# Revit family: 511_AWN_DBS_nailfin
name_source: partatom
category: Windows
units: mm (PartAtom-declared; Revit-internal decimal feet)

## family parameters
Always vertical = Yes
Cut with Voids When Loaded = No
Host = Wall
OmniClass Number = 23.30.20.00
OmniClass Title = Windows
Room Calculation Point = No
Shared = No

## types (40) — shared parameters
Default Sill Height = 31 1/2"
Wall Closure = By host

## per-type parameters (varying)
| type | Height | MLW | Width |
| 24x24 | 24" | 3" | 24" |
| 36x36 | 36" | 4 1/2" | 36" |
| 24x30 | 30" | 3" | 24" |
| 24x18 | 18" | 3" | 24" |
| 24x36 | 36" | 3" | 24" |
| 24x42 | 42" | 3" | 24" |
| 18x18 Min | 18" | 2 1/4" | 18" |
| 18x24 | 24" | 2 1/4" | 18" |
| 18x30 | 30" | 2 1/4" | 18" |
| 18x36 | 36" | 2 1/4" | 18" |
| 18x42 | 42" | 2 1/4" | 18" |
| 30x18 | 18" | 3 3/4" | 30" |
| 30x24 | 24" | 3 3/4" | 30" |
| 30x30 | 30" | 3 3/4" | 30" |
| 30x36 | 36" | 3 3/4" | 30" |
| 30x42 | 42" | 3 3/4" | 30" |
| 36x18 | 18" | 4 1/2" | 36" |
| 36x24 | 24" | 4 1/2" | 36" |
| 36x30 | 30" | 4 1/2" | 36" |
| 36x42 | 42" | 4 1/2" | 36" |
| 42x18 | 18" | 5 1/4" | 42" |
| 42x24 | 24" | 5 1/4" | 42" |
| 42x30 | 30" | 5 1/4" | 42" |
| 42x36 | 36" | 5 1/4" | 42" |
| 42x42 | 42" | 5 1/4" | 42" |
| 48x18 | 18" | 6" | 48" |
| 48x24 | 24" | 6" | 48" |
| 48x30 | 30" | 6" | 48" |
| 48x36 | 36" | 6" | 48" |
| 48x42 | 42" | 6" | 48" |
| 54x18 | 18" | 6 3/4" | 54" |
| 54x24 | 24" | 6 3/4" | 54" |
| 54x30 | 30" | 6 3/4" | 54" |
| 54x36 | 36" | 6 3/4" | 54" |
| 54x42 | 42" | 6 3/4" | 54" |
| 60x18 | 18" | 7 1/2" | 60" |
| 60x24 | 24" | 7 1/2" | 60" |
| 60x30 | 30" | 7 1/2" | 60" |
| 60x36 | 36" | 7 1/2" | 60" |
| 60x42 Max | 42" | 7 1/2" | 60" |

## geometry (parser evidence)
native form markers: Sweep x3
no freeform markers — native parametric forms only
